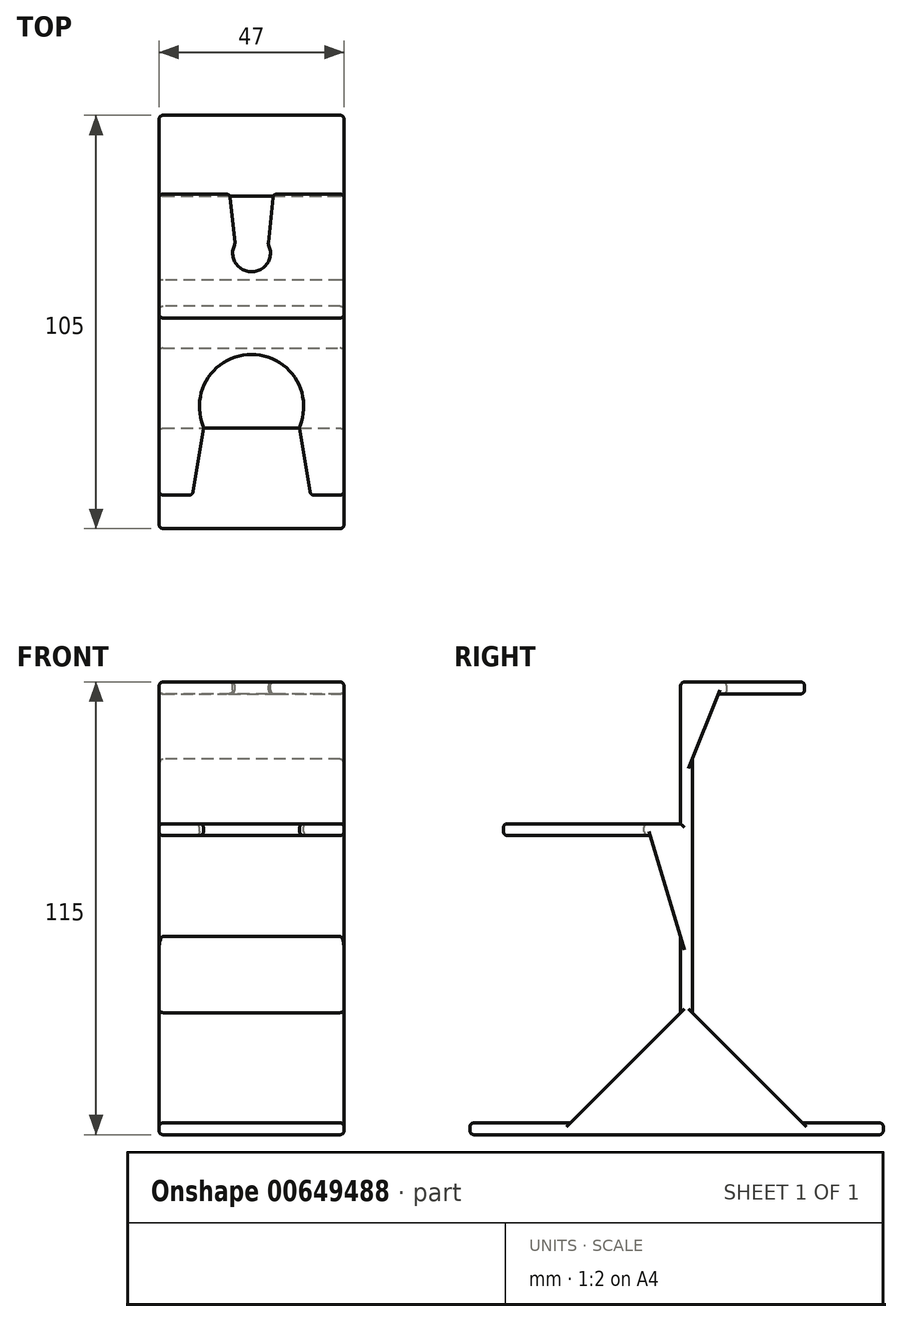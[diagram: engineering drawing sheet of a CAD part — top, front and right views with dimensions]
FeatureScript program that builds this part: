
annotation { "Feature Type Name" : "Feature", "Feature Type Description" : "" }
export const myFeature = defineFeature(function(context is Context, id is Id, definition is map)
    precondition{}
    {
        {
            var Q0;
            Q0=qCreatedBy(makeId("Right.planeOp"),FACE);
            var sketch = newSketch(context, id + "F0", { "sketchPlane" : qUnion([Q0])});
            skLineSegment(sketch, "E0", {"start": v(0, -57.5) * mm, "end": v(0, 56) * mm});
            skLineSegment(sketch, "E1", {"start": v(0, -57.5) * mm, "end": v(50, -57.5) * mm});
            skLineSegment(sketch, "E2", {"start": v(50, -57.5) * mm, "end": v(0, -57.5) * mm});
            skLineSegment(sketch, "E3", {"start": v(0, -57.5) * mm, "end": v(-55, -57.5) * mm});
            skLineSegment(sketch, "E4", {"start": v(0, -57.5) * mm, "end": v(0, 18.5) * mm});
            skLineSegment(sketch, "E5", {"start": v(0, 18.5) * mm, "end": v(-46.5, 18.5) * mm});
            skLineSegment(sketch, "E6", {"start": v(0, 56) * mm, "end": v(30, 56) * mm});
            skLineSegment(sketch, "E7.bottom", {"start": v(-46.5, 18.5) * mm, "end": v(0, 18.5) * mm});
            skLineSegment(sketch, "E7.top", {"start": v(-46.5, 18.5) * mm, "end": v(0, 18.5) * mm});
            skLineSegment(sketch, "E7.left", {"start": v(-46.5, 18.5) * mm, "end": v(-46.5, 18.5) * mm});
            skLineSegment(sketch, "E7.right", {"start": v(0, 18.5) * mm, "end": v(0, 18.5) * mm});
            skLineSegment(sketch, "E8.top", {"start": v(-46.5, 17) * mm, "end": v(0, 17) * mm});
            skLineSegment(sketch, "E8.left", {"start": v(-46.5, 18.5) * mm, "end": v(-46.5, 17) * mm});
            skLineSegment(sketch, "E8.right", {"start": v(0, 18.5) * mm, "end": v(0, 17) * mm});
            skLineSegment(sketch, "E9.bottom", {"start": v(0, 17) * mm, "end": v(-46.5, 17) * mm});
            skLineSegment(sketch, "E9.top", {"start": v(0, 20) * mm, "end": v(-46.5, 20) * mm});
            skLineSegment(sketch, "E9.left", {"start": v(0, 17) * mm, "end": v(0, 20) * mm});
            skLineSegment(sketch, "E9.right", {"start": v(-46.5, 17) * mm, "end": v(-46.5, 20) * mm});
            skLineSegment(sketch, "E10.bottom", {"start": v(0, -57.5) * mm, "end": v(1.5, -57.5) * mm});
            skLineSegment(sketch, "E10.top", {"start": v(0, 56) * mm, "end": v(1.5, 56) * mm});
            skLineSegment(sketch, "E10.right", {"start": v(1.5, -57.5) * mm, "end": v(1.5, 56) * mm});
            skLineSegment(sketch, "E11.bottom", {"start": v(1.5, 56) * mm, "end": v(-1.5, 56) * mm});
            skLineSegment(sketch, "E11.top", {"start": v(1.5, -57.5) * mm, "end": v(-1.5, -57.5) * mm});
            skLineSegment(sketch, "E11.left", {"start": v(1.5, 56) * mm, "end": v(1.5, -57.5) * mm});
            skLineSegment(sketch, "E11.right", {"start": v(-1.5, 56) * mm, "end": v(-1.5, -57.5) * mm});
            skLineSegment(sketch, "E12.bottom", {"start": v(30, 56) * mm, "end": v(0, 56) * mm});
            skLineSegment(sketch, "E12.top", {"start": v(30, 53) * mm, "end": v(0, 53) * mm});
            skLineSegment(sketch, "E12.left", {"start": v(30, 56) * mm, "end": v(30, 53) * mm});
            skLineSegment(sketch, "E12.right", {"start": v(0, 56) * mm, "end": v(0, 53) * mm});
            skLineSegment(sketch, "E13.bottom", {"start": v(-55, -57.5) * mm, "end": v(50, -57.5) * mm});
            skLineSegment(sketch, "E13.top", {"start": v(-55, -56) * mm, "end": v(50, -56) * mm});
            skLineSegment(sketch, "E13.left", {"start": v(-55, -57.5) * mm, "end": v(-55, -56) * mm});
            skLineSegment(sketch, "E13.right", {"start": v(50, -57.5) * mm, "end": v(50, -56) * mm});
            skLineSegment(sketch, "E14.bottom", {"start": v(50, -56) * mm, "end": v(-55, -56) * mm});
            skLineSegment(sketch, "E14.top", {"start": v(50, -59) * mm, "end": v(-55, -59) * mm});
            skLineSegment(sketch, "E14.left", {"start": v(50, -56) * mm, "end": v(50, -59) * mm});
            skLineSegment(sketch, "E14.right", {"start": v(-55, -56) * mm, "end": v(-55, -59) * mm});
            skSolve(sketch);
        }
        {
            var Q0;
            Q0 = qSketchRegion(id + "F0", true);
            extrude(context, id + "F1", {"entities" : qUnion([Q0]), "endBound" : BoundingType.SYMMETRIC, "oppositeDirection" : true, "depth" : 47 * mm, "offsetDistance" : 25 * mm});
        }
        {
            var Q0;
            Q0=makeQuery(id+"F1.opExtrude","SWEPT_FACE",FACE,{"disambiguationData":[OSD([sQuery(id+"F0.wireOp",EDGE,"E9.top")])]});
            var sketch = newSketch(context, id + "F2", { "sketchPlane" : qUnion([Q0])});
            skCircle(sketch, "E15", {"center": v(0, -24) * mm, "radius": 13.25 * mm});
            skLineSegment(sketch, "E16", {"start": v(-12.2, -29.18) * mm, "end": v(-15, -46.5) * mm});
            skLineSegment(sketch, "E17", {"start": v(12.2, -29.18) * mm, "end": v(15, -46.5) * mm});
            skLineSegment(sketch, "E18", {"start": v(-15, -46.5) * mm, "end": v(15, -46.5) * mm});
            skLineSegment(sketch, "E19", {"start": v(12.2, -29.18) * mm, "end": v(-12.2, -29.18) * mm});
            skSolve(sketch);
        }
        {
            var Q0;
            Q0 = qSketchRegion(id + "F2", true);
            extrude(context, id + "F3", {"entities" : qUnion([Q0]), "operationType" : NewBodyOperationType.REMOVE, "oppositeDirection" : true, "depth" : 25 * mm, "offsetDistance" : 25 * mm});
        }
        {
            var Q0;
            Q0=makeQuery(id+"F1.opExtrude","SWEPT_FACE",FACE,{"disambiguationData":[OSD([sQuery(id+"F0.wireOp",EDGE,"E11.bottom"),sQuery(id+"F0.wireOp",EDGE,"E12.bottom")])]});
            var sketch = newSketch(context, id + "F4", { "sketchPlane" : qUnion([Q0])});
            skCircle(sketch, "E20", {"center": v(0, 15.02) * mm, "radius": 4.8 * mm});
            skLineSegment(sketch, "E21", {"start": v(-4.23, 17.3) * mm, "end": v(-5.5, 30) * mm});
            skLineSegment(sketch, "E22", {"start": v(-4.23, 17.3) * mm, "end": v(4.23, 17.3) * mm});
            skLineSegment(sketch, "E23", {"start": v(4.23, 17.3) * mm, "end": v(5.5, 30) * mm});
            skLineSegment(sketch, "E24", {"start": v(5.5, 30) * mm, "end": v(-5.5, 30) * mm});
            skSolve(sketch);
        }
        {
            var Q0;
            Q0 = qSketchRegion(id + "F4", true);
            extrude(context, id + "F5", {"entities" : qUnion([Q0]), "operationType" : NewBodyOperationType.REMOVE, "oppositeDirection" : true, "depth" : 25 * mm, "offsetDistance" : 25 * mm});
        }
        {
            var Q0;
            Q0=makeQuery(id+"F1.opExtrude","CAP_FACE",FACE,{"disambiguationData":[OSD([sQuery(id+"F0.wireOp",EDGE,"E9.bottom"),sQuery(id+"F0.wireOp",EDGE,"E9.top"),sQuery(id+"F0.wireOp",EDGE,"E9.right"),sQuery(id+"F0.wireOp",EDGE,"E11.bottom"),sQuery(id+"F0.wireOp",EDGE,"E11.left"),sQuery(id+"F0.wireOp",EDGE,"E11.right"),sQuery(id+"F0.wireOp",EDGE,"E12.bottom"),sQuery(id+"F0.wireOp",EDGE,"E12.top"),sQuery(id+"F0.wireOp",EDGE,"E12.left"),sQuery(id+"F0.wireOp",EDGE,"E14.bottom"),sQuery(id+"F0.wireOp",EDGE,"E14.top"),sQuery(id+"F0.wireOp",EDGE,"E14.left"),sQuery(id+"F0.wireOp",EDGE,"E14.right")])],"isStart":false});
            var Q1;
            Q1=makeQuery(id+"F1.opExtrude","CAP_FACE",FACE,{"disambiguationData":[OSD([sQuery(id+"F0.wireOp",EDGE,"E9.bottom"),sQuery(id+"F0.wireOp",EDGE,"E9.top"),sQuery(id+"F0.wireOp",EDGE,"E9.right"),sQuery(id+"F0.wireOp",EDGE,"E11.bottom"),sQuery(id+"F0.wireOp",EDGE,"E11.left"),sQuery(id+"F0.wireOp",EDGE,"E11.right"),sQuery(id+"F0.wireOp",EDGE,"E12.bottom"),sQuery(id+"F0.wireOp",EDGE,"E12.top"),sQuery(id+"F0.wireOp",EDGE,"E12.left"),sQuery(id+"F0.wireOp",EDGE,"E14.bottom"),sQuery(id+"F0.wireOp",EDGE,"E14.top"),sQuery(id+"F0.wireOp",EDGE,"E14.left"),sQuery(id+"F0.wireOp",EDGE,"E14.right")])],"isStart":true});
            fillet(context, id + "F6", {"entities" : qUnion([Q0, Q1]), "radius" : 1 * mm, "tangentPropagation" : true, "allowEdgeOverflow" : false});
        }
        {
            var Q0;
            {var subQ0=sQuery(id+"F0.wireOp",EDGE,"E12.left");Q0=makeQuery(id+"F5.boolean.opBoolean","SPLIT",FACE,{"disambiguationData":[TD([makeQuery(id+"F5.opExtrude","SWEPT_FACE",FACE,{"disambiguationData":[OSD([sQuery(id+"F4.wireOp",EDGE,"E21")])]})])],"derivedFrom":makeQuery(id+"F1.opExtrude","SWEPT_FACE",FACE,{"disambiguationData":[OSD([subQ0])]})});}
            var Q1;
            {var subQ0=sQuery(id+"F0.wireOp",EDGE,"E12.left");Q1=makeQuery(id+"F5.boolean.opBoolean","SPLIT",FACE,{"disambiguationData":[TD([makeQuery(id+"F5.opExtrude","SWEPT_FACE",FACE,{"disambiguationData":[OSD([sQuery(id+"F4.wireOp",EDGE,"E23")])]})])],"derivedFrom":makeQuery(id+"F1.opExtrude","SWEPT_FACE",FACE,{"disambiguationData":[OSD([subQ0])]})});}
            var Q2;
            Q2=makeQuery(id+"F1.opExtrude","SWEPT_FACE",FACE,{"disambiguationData":[OSD([sQuery(id+"F0.wireOp",EDGE,"E14.left")])]});
            var Q3;
            Q3=makeQuery(id+"F1.opExtrude","SWEPT_FACE",FACE,{"disambiguationData":[OSD([sQuery(id+"F0.wireOp",EDGE,"E14.right")])]});
            var Q4;
            {var subQ1=sQuery(id+"F0.wireOp",EDGE,"E9.right");Q4=makeQuery(id+"F3.boolean.opBoolean","SPLIT",FACE,{"disambiguationData":[TD([makeQuery(id+"F3.opExtrude","SWEPT_FACE",FACE,{"disambiguationData":[OSD([sQuery(id+"F2.wireOp",EDGE,"E16")])]})])],"derivedFrom":makeQuery(id+"F1.opExtrude","SWEPT_FACE",FACE,{"disambiguationData":[OSD([subQ1])]})});}
            var Q5;
            {var subQ1=sQuery(id+"F0.wireOp",EDGE,"E9.right");Q5=makeQuery(id+"F3.boolean.opBoolean","SPLIT",FACE,{"disambiguationData":[TD([makeQuery(id+"F3.opExtrude","SWEPT_FACE",FACE,{"disambiguationData":[OSD([sQuery(id+"F2.wireOp",EDGE,"E17")])]})])],"derivedFrom":makeQuery(id+"F1.opExtrude","SWEPT_FACE",FACE,{"disambiguationData":[OSD([subQ1])]})});}
            fillet(context, id + "F7", {"entities" : qUnion([Q0, Q1, Q2, Q3, Q4, Q5]), "radius" : 1 * mm, "tangentPropagation" : true, "allowEdgeOverflow" : false});
        }
        {
            var Q0;
            Q0=makeQuery(id+"F3.boolean.opBoolean","COPY",FACE,{"derivedFrom":makeQuery(id+"F3.opExtrude","SWEPT_FACE",FACE,{"disambiguationData":[OSD([sQuery(id+"F2.wireOp",EDGE,"E15")])]})});
            var Q1;
            Q1=makeQuery(id+"F3.boolean.opBoolean","COPY",FACE,{"derivedFrom":makeQuery(id+"F3.opExtrude","SWEPT_FACE",FACE,{"disambiguationData":[OSD([sQuery(id+"F2.wireOp",EDGE,"E16")])]})});
            var Q2;
            Q2=makeQuery(id+"F3.boolean.opBoolean","COPY",FACE,{"derivedFrom":makeQuery(id+"F3.opExtrude","SWEPT_FACE",FACE,{"disambiguationData":[OSD([sQuery(id+"F2.wireOp",EDGE,"E17")])]})});
            var Q3;
            Q3=makeQuery(id+"F5.boolean.opBoolean","COPY",FACE,{"derivedFrom":makeQuery(id+"F5.opExtrude","SWEPT_FACE",FACE,{"disambiguationData":[OSD([sQuery(id+"F4.wireOp",EDGE,"E21")])]})});
            var Q4;
            Q4=makeQuery(id+"F5.boolean.opBoolean","COPY",FACE,{"derivedFrom":makeQuery(id+"F5.opExtrude","SWEPT_FACE",FACE,{"disambiguationData":[OSD([sQuery(id+"F4.wireOp",EDGE,"E20")])]})});
            var Q5;
            Q5=makeQuery(id+"F5.boolean.opBoolean","COPY",FACE,{"derivedFrom":makeQuery(id+"F5.opExtrude","SWEPT_FACE",FACE,{"disambiguationData":[OSD([sQuery(id+"F4.wireOp",EDGE,"E23")])]})});
            fillet(context, id + "F8", {"entities" : qUnion([Q0, Q1, Q2, Q3, Q4, Q5]), "radius" : 1 * mm, "tangentPropagation" : true, "allowEdgeOverflow" : false});
        }
        {
            var Q0;
            Q0=makeQuery(id+"F1.opExtrude","SWEPT_EDGE",EDGE,{"disambiguationData":[OSD([sQuery(id+"F0.wireOp",EDGE,"E11.bottom"),sQuery(id+"F0.wireOp",EDGE,"E11.right")])]});
            fillet(context, id + "F9", {"entities" : qUnion([Q0]), "radius" : 1 * mm, "tangentPropagation" : true, "allowEdgeOverflow" : false});
        }
        {
            var Q0;
            Q0=makeQuery(id+"F1.opExtrude","CAP_FACE",FACE,{"disambiguationData":[OSD([sQuery(id+"F0.wireOp",EDGE,"E9.bottom"),sQuery(id+"F0.wireOp",EDGE,"E9.top"),sQuery(id+"F0.wireOp",EDGE,"E9.right"),sQuery(id+"F0.wireOp",EDGE,"E11.bottom"),sQuery(id+"F0.wireOp",EDGE,"E11.left"),sQuery(id+"F0.wireOp",EDGE,"E11.right"),sQuery(id+"F0.wireOp",EDGE,"E12.bottom"),sQuery(id+"F0.wireOp",EDGE,"E12.top"),sQuery(id+"F0.wireOp",EDGE,"E12.left"),sQuery(id+"F0.wireOp",EDGE,"E14.bottom"),sQuery(id+"F0.wireOp",EDGE,"E14.top"),sQuery(id+"F0.wireOp",EDGE,"E14.left"),sQuery(id+"F0.wireOp",EDGE,"E14.right")])],"isStart":false});
            var sketch = newSketch(context, id + "F10", { "sketchPlane" : qUnion([Q0])});
            skLineSegment(sketch, "E25", {"start": v(30.5, -57) * mm, "end": v(0.5, -57) * mm});
            skLineSegment(sketch, "E26", {"start": v(0.5, -57) * mm, "end": v(0.5, -27) * mm});
            skLineSegment(sketch, "E27", {"start": v(0.5, -27) * mm, "end": v(30.5, -57) * mm});
            skLineSegment(sketch, "E28", {"start": v(-0.5, -57) * mm, "end": v(-0.5, -27) * mm});
            skLineSegment(sketch, "E29", {"start": v(-0.5, -27) * mm, "end": v(-30.5, -57) * mm});
            skLineSegment(sketch, "E30", {"start": v(-30.5, -57) * mm, "end": v(-0.5, -57) * mm});
            skLineSegment(sketch, "E31", {"start": v(0.5, 18) * mm, "end": v(9.5, 18) * mm});
            skLineSegment(sketch, "E32", {"start": v(9.5, 18) * mm, "end": v(0.5, -12) * mm});
            skLineSegment(sketch, "E33", {"start": v(0.5, -12) * mm, "end": v(0.5, 18) * mm});
            skLineSegment(sketch, "E34", {"start": v(-0.5, 54) * mm, "end": v(-8.5, 54) * mm});
            skLineSegment(sketch, "E35", {"start": v(-8.5, 54) * mm, "end": v(-0.5, 34) * mm});
            skLineSegment(sketch, "E36", {"start": v(-0.5, 34) * mm, "end": v(-0.5, 54) * mm});
            skSolve(sketch);
        }
        {
            var Q0;
            Q0 = qSketchRegion(id + "F10", true);
            extrude(context, id + "F11", {"entities" : qUnion([Q0]), "operationType" : NewBodyOperationType.ADD, "oppositeDirection" : true, "depth" : 47 * mm, "offsetDistance" : 25 * mm});
        }
    });
